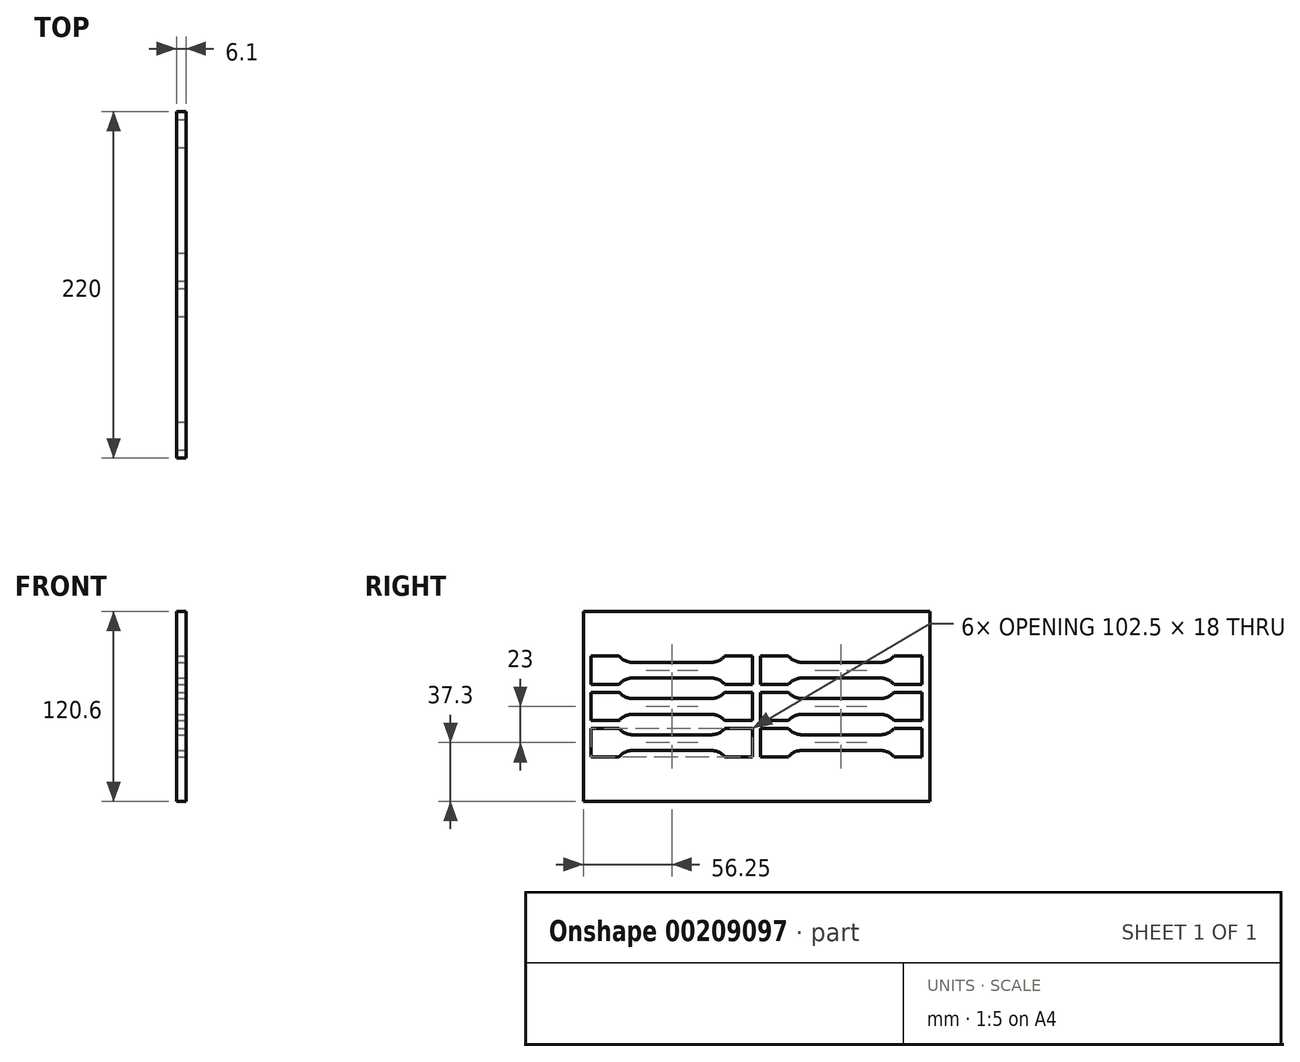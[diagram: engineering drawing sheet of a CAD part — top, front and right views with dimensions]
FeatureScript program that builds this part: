
annotation { "Feature Type Name" : "Feature", "Feature Type Description" : "" }
export const myFeature = defineFeature(function(context is Context, id is Id, definition is map)
    precondition{}
    {
        {
            var Q0;
            Q0=qCreatedBy(makeId("Front.planeOp"),FACE);
            var sketch = newSketch(context, id + "F0", { "sketchPlane" : qUnion([Q0])});
            skLineSegment(sketch, "E0.left", {"start": v(3.05, -60.3) * mm, "end": v(3.05, 60.3) * mm});
            skLineSegment(sketch, "E0.right", {"start": v(-3.05, -60.3) * mm, "end": v(-3.05, 60.3) * mm});
            skPoint(sketch, "E0.middle", {"position": v(0, 0) * mm});
            skLineSegment(sketch, "E1.top", {"start": v(76, 76) * mm, "end": v(-76, 76) * mm});
            skLineSegment(sketch, "E1.left", {"start": v(76, 69.2) * mm, "end": v(76, 76) * mm});
            skLineSegment(sketch, "E1.right", {"start": v(-76, 69.2) * mm, "end": v(-76, 76) * mm});
            skPoint(sketch, "E1.middle", {"position": v(0, 72.6) * mm});
            skPoint(sketch, "E1.middle.positionSnap0", {"position": v(0, 69.2) * mm});
            skPoint(sketch, "E1.centerSnap0", {"position": v(0, 69.2) * mm});
            skLineSegment(sketch, "E2.top", {"start": v(76, -76) * mm, "end": v(-76, -76) * mm});
            skLineSegment(sketch, "E2.left", {"start": v(76, -69.2) * mm, "end": v(76, -76) * mm});
            skLineSegment(sketch, "E2.right", {"start": v(-76, -69.2) * mm, "end": v(-76, -76) * mm});
            skPoint(sketch, "E2.middle", {"position": v(0, -72.6) * mm});
            skLineSegment(sketch, "E3", {"start": v(-76, 69.2) * mm, "end": v(-11.95, 69.2) * mm});
            skLineSegment(sketch, "E4", {"start": v(11.95, 69.2) * mm, "end": v(76, 69.2) * mm});
            skLineSegment(sketch, "E5", {"start": v(11.95, -69.2) * mm, "end": v(76, -69.2) * mm});
            skLineSegment(sketch, "E6", {"start": v(-11.95, -69.2) * mm, "end": v(-76, -69.2) * mm});
            skPoint(sketch, "E7.visualSharp", {"position": v(-3.05, 69.2) * mm});
            skArc(sketch, "E7.filletArc", {"start": v(-3.05, 60.3) * mm, "mid": v(-5.66, 66.6) * mm, "end": v(-11.95, 69.2) * mm});
            skPoint(sketch, "E8.visualSharp", {"position": v(3.05, 69.2) * mm});
            skArc(sketch, "E8.filletArc", {"start": v(11.95, 69.2) * mm, "mid": v(5.66, 66.6) * mm, "end": v(3.05, 60.3) * mm});
            skPoint(sketch, "E9.visualSharp", {"position": v(-3.05, -69.2) * mm});
            skArc(sketch, "E9.filletArc", {"start": v(-11.95, -69.2) * mm, "mid": v(-5.66, -66.6) * mm, "end": v(-3.05, -60.3) * mm});
            skPoint(sketch, "E10.visualSharp", {"position": v(3.05, -69.2) * mm});
            skArc(sketch, "E10.filletArc", {"start": v(3.05, -60.3) * mm, "mid": v(5.66, -66.6) * mm, "end": v(11.95, -69.2) * mm});
            skPoint(sketch, "E11.startSnap0", {"position": v(-5.66, 66.6) * mm});
            skPoint(sketch, "E11.endSnap0", {"position": v(-5.66, 66.6) * mm});
            skPoint(sketch, "E12.startSnap0", {"position": v(-5.66, -66.6) * mm});
            skSolve(sketch);
        }
        {
            var Q0;
            Q0=makeQuery(id+"F0.imprint","IMPRINT",FACE,{"disambiguationData":[TD([[makeQuery(id+"F0.imprint","IMPRINT",EDGE,{"derivedFrom":sQuery(id+"F0.wireOp",EDGE,"E0.left")}),1.0]])]});
            extrude(context, id + "F1", {"entities" : qUnion([Q0]), "depth" : 220 * mm, "symmetric" : true});
        }
        {
            var Q0;
            Q0=makeQuery(id+"F1.opExtrude","SWEPT_FACE",FACE,{"disambiguationData":[OSD([sQuery(id+"F0.wireOp",EDGE,"E0.left")])]});
            var sketch = newSketch(context, id + "F2", { "sketchPlane" : qUnion([Q0])});
            skLineSegment(sketch, "E13.left", {"start": v(-2.5, -9) * mm, "end": v(-2.5, 9) * mm});
            skLineSegment(sketch, "E13.right", {"start": v(-105, -9) * mm, "end": v(-105, 9) * mm});
            skPoint(sketch, "E13.middle", {"position": v(-53.75, 0) * mm});
            skLineSegment(sketch, "E14.bottom", {"start": v(-28.75, -5) * mm, "end": v(-78.75, -5) * mm});
            skLineSegment(sketch, "E14.top", {"start": v(-28.75, 5) * mm, "end": v(-78.75, 5) * mm});
            skArc(sketch, "E15", {"start": v(-28.75, 5) * mm, "mid": v(-24.06, 6.05) * mm, "end": v(-20.26, 9) * mm});
            skArc(sketch, "E16", {"start": v(-28.75, -5) * mm, "mid": v(-24.06, -6.05) * mm, "end": v(-20.26, -9) * mm});
            skArc(sketch, "E17", {"start": v(-78.75, -5) * mm, "mid": v(-83.44, -6.05) * mm, "end": v(-87.24, -9) * mm});
            skArc(sketch, "E18", {"start": v(-78.75, 5) * mm, "mid": v(-83.44, 6.05) * mm, "end": v(-87.24, 9) * mm});
            skLineSegment(sketch, "E19", {"start": v(-105, 9) * mm, "end": v(-87.24, 9) * mm});
            skLineSegment(sketch, "E20", {"start": v(-105, -9) * mm, "end": v(-87.24, -9) * mm});
            skLineSegment(sketch, "E21", {"start": v(-20.26, -9) * mm, "end": v(-2.5, -9) * mm});
            skLineSegment(sketch, "E22", {"start": v(-20.26, 9) * mm, "end": v(-2.5, 9) * mm});
            skPoint(sketch, "E23.MirrorP", {"position": v(-53.75, 23) * mm});
            skArc(sketch, "E24.MirrorCS", {"start": v(-28.75, 28) * mm, "mid": v(-24.06, 29.05) * mm, "end": v(-20.26, 32) * mm});
            skLineSegment(sketch, "E25.MirrorCS", {"start": v(-105, 14) * mm, "end": v(-87.24, 14) * mm});
            skLineSegment(sketch, "E26.MirrorCS", {"start": v(-28.75, 18) * mm, "end": v(-78.75, 18) * mm});
            skLineSegment(sketch, "E27.MirrorCS", {"start": v(-105, 32) * mm, "end": v(-105, 14) * mm});
            skLineSegment(sketch, "E28.MirrorCS", {"start": v(-2.5, 32) * mm, "end": v(-2.5, 14) * mm});
            skArc(sketch, "E29.MirrorCS", {"start": v(-78.75, 28) * mm, "mid": v(-83.44, 29.05) * mm, "end": v(-87.24, 32) * mm});
            skLineSegment(sketch, "E30.MirrorCS", {"start": v(-20.26, 14) * mm, "end": v(-2.5, 14) * mm});
            skLineSegment(sketch, "E31.MirrorCS", {"start": v(-28.75, 28) * mm, "end": v(-78.75, 28) * mm});
            skLineSegment(sketch, "E32.MirrorCS", {"start": v(-105, 32) * mm, "end": v(-87.24, 32) * mm});
            skLineSegment(sketch, "E33.MirrorCS", {"start": v(-20.26, 32) * mm, "end": v(-2.5, 32) * mm});
            skArc(sketch, "E34.MirrorCS", {"start": v(-78.75, 18) * mm, "mid": v(-83.44, 16.95) * mm, "end": v(-87.24, 14) * mm});
            skArc(sketch, "E35.MirrorCS", {"start": v(-28.75, 18) * mm, "mid": v(-24.06, 16.95) * mm, "end": v(-20.26, 14) * mm});
            skPoint(sketch, "E36.MirrorP", {"position": v(-53.75, -23) * mm});
            skLineSegment(sketch, "E37.MirrorCS", {"start": v(-20.26, -32) * mm, "end": v(-2.5, -32) * mm});
            skLineSegment(sketch, "E38.MirrorCS", {"start": v(-2.5, -14) * mm, "end": v(-2.5, -32) * mm});
            skLineSegment(sketch, "E39.MirrorCS", {"start": v(-28.75, -28) * mm, "end": v(-78.75, -28) * mm});
            skLineSegment(sketch, "E40.MirrorCS", {"start": v(-28.75, -18) * mm, "end": v(-78.75, -18) * mm});
            skArc(sketch, "E41.MirrorCS", {"start": v(-28.75, -18) * mm, "mid": v(-24.06, -16.95) * mm, "end": v(-20.26, -14) * mm});
            skArc(sketch, "E42.MirrorCS", {"start": v(-78.75, -18) * mm, "mid": v(-83.44, -16.95) * mm, "end": v(-87.24, -14) * mm});
            skLineSegment(sketch, "E43.MirrorCS", {"start": v(-20.26, -14) * mm, "end": v(-2.5, -14) * mm});
            skLineSegment(sketch, "E44.MirrorCS", {"start": v(-105, -32) * mm, "end": v(-87.24, -32) * mm});
            skArc(sketch, "E45.MirrorCS", {"start": v(-78.75, -28) * mm, "mid": v(-83.44, -29.05) * mm, "end": v(-87.24, -32) * mm});
            skLineSegment(sketch, "E46.MirrorCS", {"start": v(-105, -14) * mm, "end": v(-105, -32) * mm});
            skLineSegment(sketch, "E47.MirrorCS", {"start": v(-105, -14) * mm, "end": v(-87.24, -14) * mm});
            skArc(sketch, "E48.MirrorCS", {"start": v(-28.75, -28) * mm, "mid": v(-24.06, -29.05) * mm, "end": v(-20.26, -32) * mm});
            skArc(sketch, "E49.MirrorCS", {"start": v(28.75, 28) * mm, "mid": v(24.06, 29.05) * mm, "end": v(20.26, 32) * mm});
            skPoint(sketch, "E50.MirrorP", {"position": v(53.75, 0) * mm});
            skPoint(sketch, "E51.MirrorP", {"position": v(53.75, -23) * mm});
            skPoint(sketch, "E52.MirrorP", {"position": v(53.75, 23) * mm});
            skLineSegment(sketch, "E53.MirrorCS", {"start": v(28.75, -28) * mm, "end": v(78.75, -28) * mm});
            skLineSegment(sketch, "E54.MirrorCS", {"start": v(20.26, 32) * mm, "end": v(2.5, 32) * mm});
            skArc(sketch, "E55.MirrorCS", {"start": v(28.75, -5) * mm, "mid": v(24.06, -6.05) * mm, "end": v(20.26, -9) * mm});
            skArc(sketch, "E56.MirrorCS", {"start": v(28.75, -18) * mm, "mid": v(24.06, -16.95) * mm, "end": v(20.26, -14) * mm});
            skLineSegment(sketch, "E57.MirrorCS", {"start": v(20.26, -32) * mm, "end": v(2.5, -32) * mm});
            skLineSegment(sketch, "E58.MirrorCS", {"start": v(105, -9) * mm, "end": v(105, 9) * mm});
            skLineSegment(sketch, "E59.MirrorCS", {"start": v(28.75, 18) * mm, "end": v(78.75, 18) * mm});
            skLineSegment(sketch, "E60.MirrorCS", {"start": v(2.5, -9) * mm, "end": v(2.5, 9) * mm});
            skLineSegment(sketch, "E61.MirrorCS", {"start": v(2.5, -14) * mm, "end": v(2.5, -32) * mm});
            skLineSegment(sketch, "E62.MirrorCS", {"start": v(105, -9) * mm, "end": v(87.24, -9) * mm});
            skLineSegment(sketch, "E63.MirrorCS", {"start": v(105, -14) * mm, "end": v(87.24, -14) * mm});
            skLineSegment(sketch, "E64.MirrorCS", {"start": v(20.26, 9) * mm, "end": v(2.5, 9) * mm});
            skLineSegment(sketch, "E65.MirrorCS", {"start": v(105, 9) * mm, "end": v(87.24, 9) * mm});
            skLineSegment(sketch, "E66.MirrorCS", {"start": v(20.26, -14) * mm, "end": v(2.5, -14) * mm});
            skArc(sketch, "E67.MirrorCS", {"start": v(78.75, -18) * mm, "mid": v(83.44, -16.95) * mm, "end": v(87.24, -14) * mm});
            skLineSegment(sketch, "E68.MirrorCS", {"start": v(20.26, 14) * mm, "end": v(2.5, 14) * mm});
            skLineSegment(sketch, "E69.MirrorCS", {"start": v(105, -14) * mm, "end": v(105, -32) * mm});
            skArc(sketch, "E70.MirrorCS", {"start": v(78.75, 18) * mm, "mid": v(83.44, 16.95) * mm, "end": v(87.24, 14) * mm});
            skLineSegment(sketch, "E71.MirrorCS", {"start": v(28.75, 28) * mm, "end": v(78.75, 28) * mm});
            skArc(sketch, "E72.MirrorCS", {"start": v(28.75, -28) * mm, "mid": v(24.06, -29.05) * mm, "end": v(20.26, -32) * mm});
            skLineSegment(sketch, "E73.MirrorCS", {"start": v(28.75, -18) * mm, "end": v(78.75, -18) * mm});
            skArc(sketch, "E74.MirrorCS", {"start": v(78.75, -28) * mm, "mid": v(83.44, -29.05) * mm, "end": v(87.24, -32) * mm});
            skArc(sketch, "E75.MirrorCS", {"start": v(78.75, 28) * mm, "mid": v(83.44, 29.05) * mm, "end": v(87.24, 32) * mm});
            skArc(sketch, "E76.MirrorCS", {"start": v(78.75, 5) * mm, "mid": v(83.44, 6.05) * mm, "end": v(87.24, 9) * mm});
            skLineSegment(sketch, "E77.MirrorCS", {"start": v(2.5, 32) * mm, "end": v(2.5, 14) * mm});
            skLineSegment(sketch, "E78.MirrorCS", {"start": v(105, 32) * mm, "end": v(87.24, 32) * mm});
            skArc(sketch, "E79.MirrorCS", {"start": v(28.75, 18) * mm, "mid": v(24.06, 16.95) * mm, "end": v(20.26, 14) * mm});
            skLineSegment(sketch, "E80.MirrorCS", {"start": v(20.26, -9) * mm, "end": v(2.5, -9) * mm});
            skLineSegment(sketch, "E81.MirrorCS", {"start": v(105, -32) * mm, "end": v(87.24, -32) * mm});
            skLineSegment(sketch, "E82.MirrorCS", {"start": v(28.75, 5) * mm, "end": v(78.75, 5) * mm});
            skLineSegment(sketch, "E83.MirrorCS", {"start": v(105, 32) * mm, "end": v(105, 14) * mm});
            skArc(sketch, "E84.MirrorCS", {"start": v(78.75, -5) * mm, "mid": v(83.44, -6.05) * mm, "end": v(87.24, -9) * mm});
            skLineSegment(sketch, "E85.MirrorCS", {"start": v(28.75, -5) * mm, "end": v(78.75, -5) * mm});
            skLineSegment(sketch, "E86.MirrorCS", {"start": v(105, 14) * mm, "end": v(87.24, 14) * mm});
            skArc(sketch, "E87.MirrorCS", {"start": v(28.75, 5) * mm, "mid": v(24.06, 6.05) * mm, "end": v(20.26, 9) * mm});
            skSolve(sketch);
        }
        {
            var Q0;
            Q0 = qSketchRegion(id + "F2", true);
            extrude(context, id + "F3", {"entities" : qUnion([Q0]), "operationType" : NewBodyOperationType.REMOVE, "oppositeDirection" : true, "depth" : 6.1 * mm});
        }
        {
            var Q0;
            Q0=makeQuery(id+"F1.opExtrude","SWEPT_FACE",FACE,{"disambiguationData":[OSD([sQuery(id+"F0.wireOp",EDGE,"E0.left")])]});
            var sketch = newSketch(context, id + "F4", { "sketchPlane" : qUnion([Q0])});
            skLineSegment(sketch, "E88.bottom", {"start": v(110, 60.3) * mm, "end": v(-110, 60.3) * mm});
            skLineSegment(sketch, "E88.top", {"start": v(110, 76) * mm, "end": v(-110, 76) * mm});
            skLineSegment(sketch, "E88.left", {"start": v(110, 60.3) * mm, "end": v(110, 76) * mm});
            skLineSegment(sketch, "E88.right", {"start": v(-110, 60.3) * mm, "end": v(-110, 76) * mm});
            skPoint(sketch, "E88.middle", {"position": v(0, 68.15) * mm});
            skPoint(sketch, "E88.middle.positionSnap0", {"position": v(0, 60.3) * mm});
            skPoint(sketch, "E88.centerSnap0", {"position": v(0, 60.3) * mm});
            skPoint(sketch, "E89.MirrorP", {"position": v(0, -60.3) * mm});
            skPoint(sketch, "E90.MirrorP", {"position": v(0, -68.15) * mm});
            skLineSegment(sketch, "E91.MirrorCS", {"start": v(110, -60.3) * mm, "end": v(-110, -60.3) * mm});
            skLineSegment(sketch, "E92.MirrorCS", {"start": v(110, -76) * mm, "end": v(-110, -76) * mm});
            skLineSegment(sketch, "E93.MirrorCS", {"start": v(110, -60.3) * mm, "end": v(110, -76) * mm});
            skLineSegment(sketch, "E94.MirrorCS", {"start": v(-110, -60.3) * mm, "end": v(-110, -76) * mm});
            skSolve(sketch);
        }
        {
            var Q0;
            Q0=makeQuery(id+"F4.imprint","IMPRINT",FACE,{"disambiguationData":[TD([[makeQuery(id+"F4.imprint","IMPRINT",EDGE,{"derivedFrom":sQuery(id+"F4.wireOp",EDGE,"E88.bottom")}),1.0]])]});
            var Q1;
            Q1=makeQuery(id+"F4.imprint","IMPRINT",FACE,{"disambiguationData":[TD([[makeQuery(id+"F4.imprint","IMPRINT",EDGE,{"derivedFrom":sQuery(id+"F4.wireOp",EDGE,"E91.MirrorCS")}),-1.0]])]});
            extrude(context, id + "F5", {"entities" : qUnion([Q0, Q1]), "operationType" : NewBodyOperationType.REMOVE, "depth" : 200 * mm, "symmetric" : true});
        }
    });
